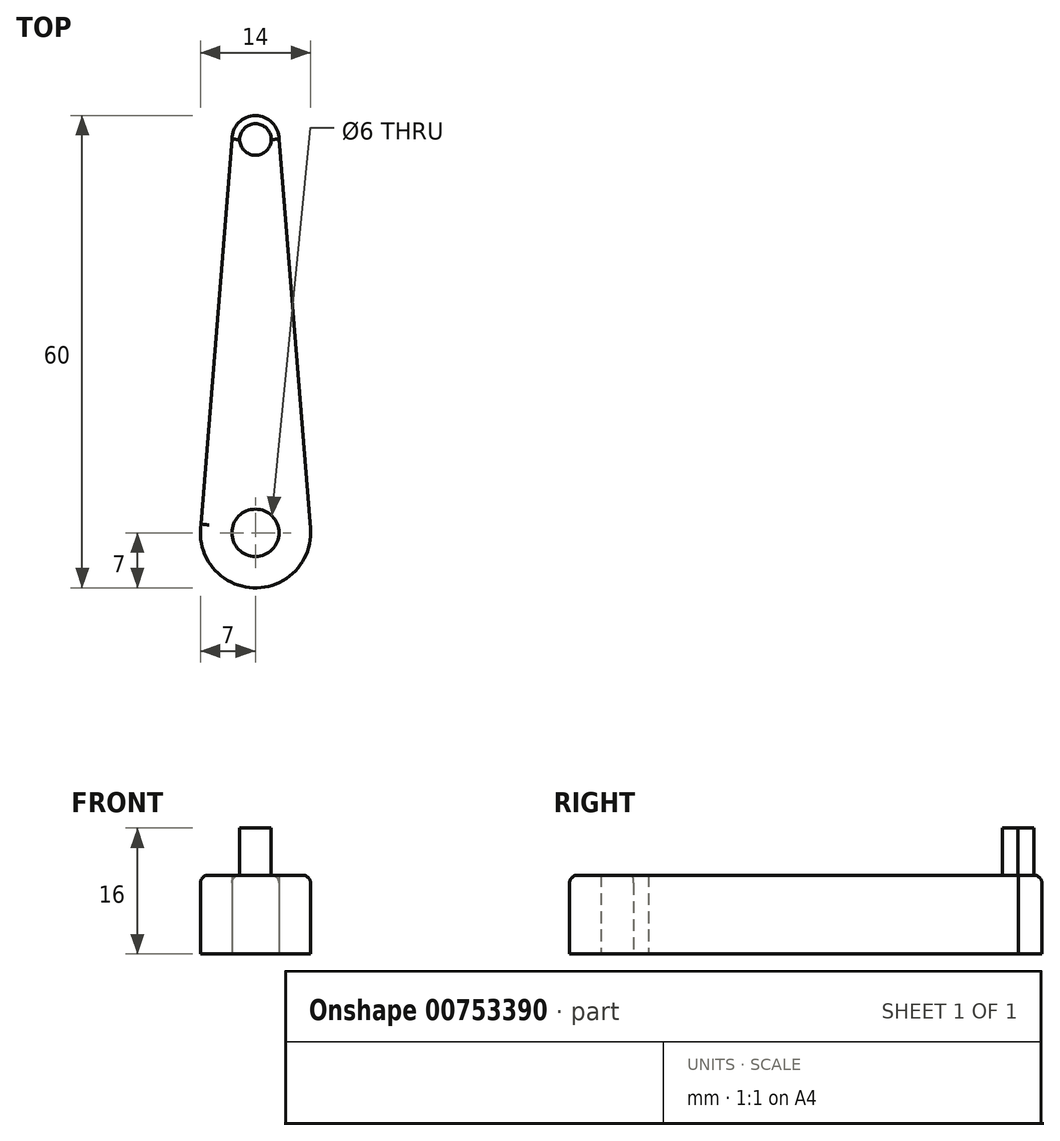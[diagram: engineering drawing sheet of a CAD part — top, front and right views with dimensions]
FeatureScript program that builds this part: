
annotation { "Feature Type Name" : "Feature", "Feature Type Description" : "" }
export const myFeature = defineFeature(function(context is Context, id is Id, definition is map)
    precondition{}
    {
        {
            var Q0;
            Q0=qCreatedBy(makeId("Top.planeOp"),FACE);
            var sketch = newSketch(context, id + "F0", { "sketchPlane" : qUnion([Q0])});
            skArc(sketch, "E0", {"start": v(-6.91, 1.11) * mm, "mid": v(-0.28, -7) * mm, "end": v(6.98, 0.56) * mm});
            skArc(sketch, "E1", {"start": v(3, 50) * mm, "mid": v(0, 53) * mm, "end": v(-3, 50) * mm});
            skLineSegment(sketch, "E2", {"start": v(3, 50) * mm, "end": v(7.02, 0) * mm});
            skLineSegment(sketch, "E3", {"start": v(-3, 50) * mm, "end": v(-7, 0) * mm});
            skLineSegment(sketch, "E4", {"start": v(0, 50) * mm, "end": v(0, 0) * mm, "construction": true});
            skLineSegment(sketch, "E5", {"start": v(0, 50) * mm, "end": v(-28.97, 50) * mm, "construction": true});
            skLineSegment(sketch, "E6", {"start": v(0, 0) * mm, "end": v(-28.62, 0) * mm, "construction": true});
            skSolve(sketch);
        }
        {
            var Q0;
            Q0 = qSketchRegion(id + "F0", true);
            extrude(context, id + "F1", {"entities" : qUnion([Q0]), "depth" : 10 * mm, "offsetDistance" : 25 * mm});
        }
        {
            var Q0;
            Q0=makeQuery(id+"F1.opExtrude","CAP_FACE",FACE,{"disambiguationData":[OSD([sQuery(id+"F0.wireOp",EDGE,"E0"),sQuery(id+"F0.wireOp",EDGE,"E1"),sQuery(id+"F0.wireOp",EDGE,"E2"),sQuery(id+"F0.wireOp",EDGE,"E3")])],"isStart":true});
            var sketch = newSketch(context, id + "F2", { "sketchPlane" : qUnion([Q0])});
            skCircle(sketch, "E7", {"center": v(0, 0) * mm, "radius": 3 * mm});
            skSolve(sketch);
        }
        {
            var Q0;
            Q0=makeQuery(id+"F2.imprint","IMPRINT",FACE,{"disambiguationData":[TD([[makeQuery(id+"F2.imprint","IMPRINT",EDGE,{"derivedFrom":sQuery(id+"F2.wireOp",EDGE,"E7")}),1.0]])]});
            extrude(context, id + "F3", {"entities" : qUnion([Q0]), "operationType" : NewBodyOperationType.REMOVE, "oppositeDirection" : true, "depth" : 25 * mm, "offsetDistance" : 25 * mm});
        }
        {
            var Q0;
            Q0=makeQuery(id+"F1.opExtrude","CAP_EDGE",EDGE,{"disambiguationData":[OSD([sQuery(id+"F0.wireOp",EDGE,"E2")])],"isStart":false});
            var Q1;
            Q1=makeQuery(id+"F1.opExtrude","CAP_EDGE",EDGE,{"disambiguationData":[OSD([sQuery(id+"F0.wireOp",EDGE,"E3")])],"isStart":false});
            var Q2;
            Q2=makeQuery(id+"F1.opExtrude","CAP_EDGE",EDGE,{"disambiguationData":[OSD([sQuery(id+"F0.wireOp",EDGE,"E1")])],"isStart":false});
            fillet(context, id + "F4", {"entities" : qUnion([Q0, Q1, Q2]), "radius" : 1 * mm, "tangentPropagation" : true, "allowEdgeOverflow" : false});
        }
        {
            var Q0;
            Q0=makeQuery(id+"F1.opExtrude","CAP_FACE",FACE,{"disambiguationData":[OSD([sQuery(id+"F0.wireOp",EDGE,"E0"),sQuery(id+"F0.wireOp",EDGE,"E1"),sQuery(id+"F0.wireOp",EDGE,"E2"),sQuery(id+"F0.wireOp",EDGE,"E3")])],"isStart":false});
            var sketch = newSketch(context, id + "F5", { "sketchPlane" : qUnion([Q0])});
            skCircle(sketch, "E8", {"center": v(0, 49.96) * mm, "radius": 2 * mm});
            skSolve(sketch);
        }
        {
            var Q0;
            Q0=makeQuery(id+"F5.imprint","IMPRINT",FACE,{"disambiguationData":[TD([[makeQuery(id+"F5.imprint","IMPRINT",EDGE,{"derivedFrom":sQuery(id+"F5.wireOp",EDGE,"E8")}),1.0]])]});
            extrude(context, id + "F6", {"entities" : qUnion([Q0]), "operationType" : NewBodyOperationType.ADD, "depth" : 6 * mm, "offsetDistance" : 25 * mm});
        }
    });
